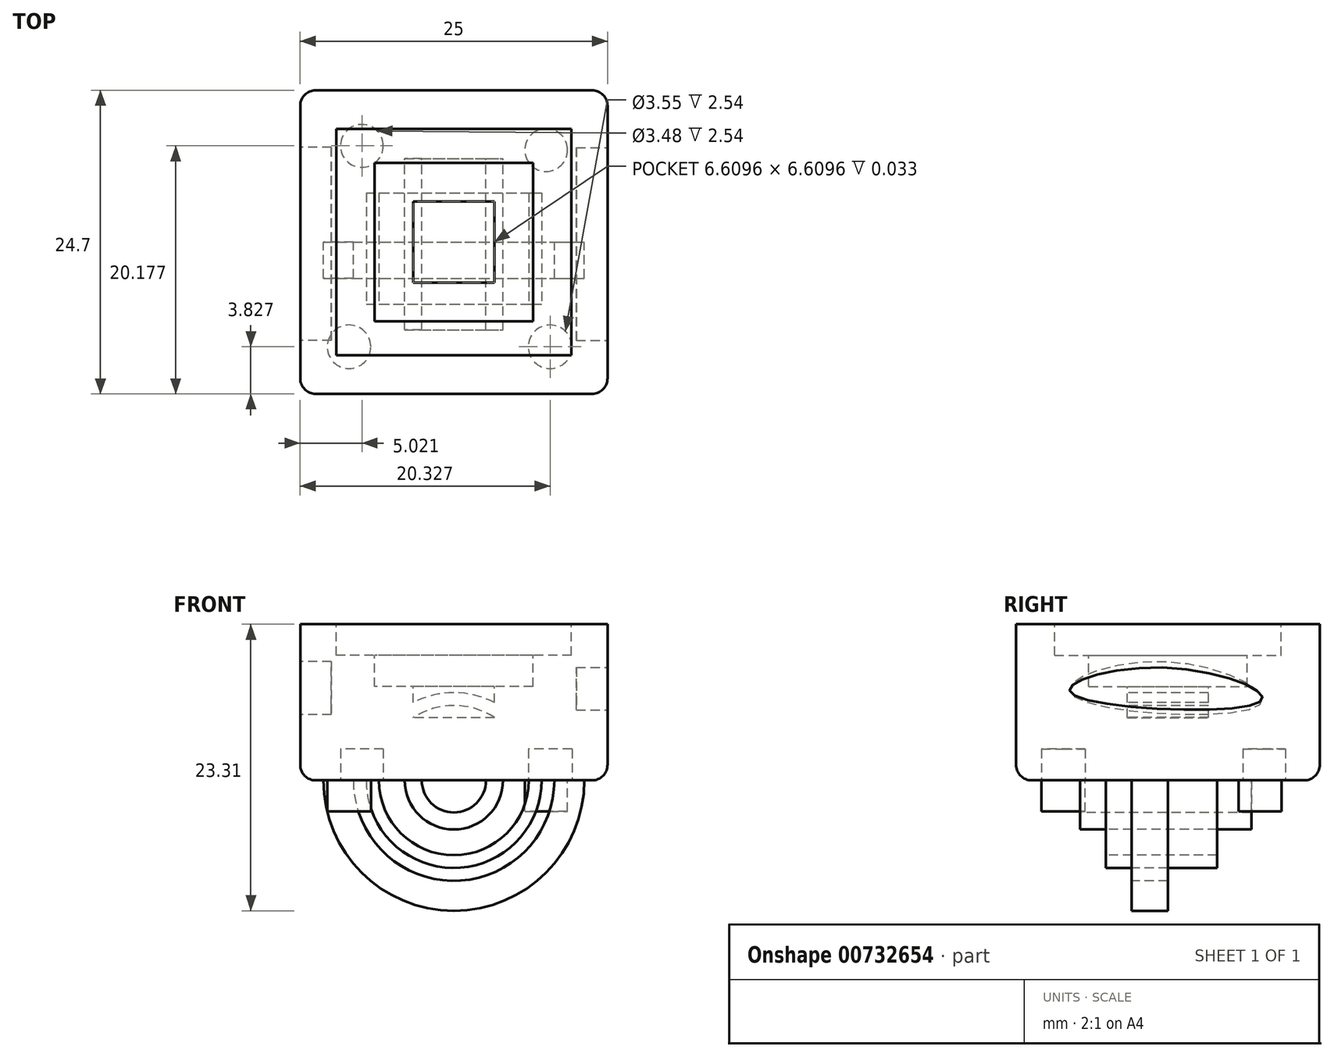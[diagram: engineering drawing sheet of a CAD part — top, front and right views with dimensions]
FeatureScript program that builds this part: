
annotation { "Feature Type Name" : "Feature", "Feature Type Description" : "" }
export const myFeature = defineFeature(function(context is Context, id is Id, definition is map)
    precondition{}
    {
        {
            var Q0;
            Q0=qCreatedBy(makeId("Top.planeOp"),FACE);
            var sketch = newSketch(context, id + "F0", { "sketchPlane" : qUnion([Q0])});
            skLineSegment(sketch, "E0.bottom", {"start": v(12.5, -12.35) * mm, "end": v(-12.5, -12.35) * mm});
            skLineSegment(sketch, "E0.top", {"start": v(12.5, 12.35) * mm, "end": v(-12.5, 12.35) * mm});
            skLineSegment(sketch, "E0.left", {"start": v(12.5, -12.35) * mm, "end": v(12.5, 12.35) * mm});
            skLineSegment(sketch, "E0.right", {"start": v(-12.5, -12.35) * mm, "end": v(-12.5, 12.35) * mm});
            skPoint(sketch, "E0.middle", {"position": v(0, 0) * mm});
            skSolve(sketch);
        }
        {
            var Q0;
            Q0=makeQuery(id+"F0.imprint","IMPRINT",FACE,{"disambiguationData":[TD([[makeQuery(id+"F0.imprint","IMPRINT",EDGE,{"derivedFrom":sQuery(id+"F0.wireOp",EDGE,"E0.bottom")}),-1.0]])]});
            extrude(context, id + "F1", {"entities" : qUnion([Q0]), "depth" : 12.7 * mm, "offsetDistance" : 25.4 * mm});
        }
        {
            var Q0;
            Q0=makeQuery(id+"F1.opExtrude","CAP_FACE",FACE,{"disambiguationData":[OSD([sQuery(id+"F0.wireOp",EDGE,"E0.bottom"),sQuery(id+"F0.wireOp",EDGE,"E0.top"),sQuery(id+"F0.wireOp",EDGE,"E0.left"),sQuery(id+"F0.wireOp",EDGE,"E0.right")])],"isStart":false});
            var sketch = newSketch(context, id + "F2", { "sketchPlane" : qUnion([Q0])});
            skLineSegment(sketch, "E1.bottom", {"start": v(9.57, -9.22) * mm, "end": v(-9.57, -9.22) * mm});
            skLineSegment(sketch, "E1.top", {"start": v(9.57, 9.22) * mm, "end": v(-9.57, 9.22) * mm});
            skLineSegment(sketch, "E1.left", {"start": v(9.57, -9.22) * mm, "end": v(9.57, 9.22) * mm});
            skLineSegment(sketch, "E1.right", {"start": v(-9.57, -9.22) * mm, "end": v(-9.57, 9.22) * mm});
            skPoint(sketch, "E1.middle", {"position": v(0, 0) * mm});
            skSolve(sketch);
        }
        {
            var Q0;
            Q0=makeQuery(id+"F2.imprint","IMPRINT",FACE,{"disambiguationData":[TD([[makeQuery(id+"F2.imprint","IMPRINT",EDGE,{"derivedFrom":sQuery(id+"F2.wireOp",EDGE,"E1.bottom")}),-1.0]])]});
            extrude(context, id + "F3", {"entities" : qUnion([Q0]), "operationType" : NewBodyOperationType.REMOVE, "oppositeDirection" : true, "depth" : 2.54 * mm, "offsetDistance" : 25.4 * mm});
        }
        {
            var Q0;
            Q0=makeQuery(id+"F3.boolean.opBoolean","COPY",FACE,{"derivedFrom":makeQuery(id+"F3.opExtrude","CAP_FACE",FACE,{"disambiguationData":[OSD([sQuery(id+"F2.wireOp",EDGE,"E1.bottom"),sQuery(id+"F2.wireOp",EDGE,"E1.top"),sQuery(id+"F2.wireOp",EDGE,"E1.left"),sQuery(id+"F2.wireOp",EDGE,"E1.right")])],"isStart":false})});
            var sketch = newSketch(context, id + "F4", { "sketchPlane" : qUnion([Q0])});
            skLineSegment(sketch, "E2.bottom", {"start": v(6.44, -6.44) * mm, "end": v(-6.44, -6.44) * mm});
            skLineSegment(sketch, "E2.top", {"start": v(6.44, 6.44) * mm, "end": v(-6.44, 6.44) * mm});
            skLineSegment(sketch, "E2.left", {"start": v(6.44, -6.44) * mm, "end": v(6.44, 6.44) * mm});
            skLineSegment(sketch, "E2.right", {"start": v(-6.44, -6.44) * mm, "end": v(-6.44, 6.44) * mm});
            skPoint(sketch, "E2.middle", {"position": v(0, 0) * mm});
            skSolve(sketch);
        }
        {
            var Q0;
            Q0=makeQuery(id+"F4.imprint","IMPRINT",FACE,{"disambiguationData":[TD([[makeQuery(id+"F4.imprint","IMPRINT",EDGE,{"derivedFrom":sQuery(id+"F4.wireOp",EDGE,"E2.bottom")}),-1.0]])]});
            extrude(context, id + "F5", {"entities" : qUnion([Q0]), "operationType" : NewBodyOperationType.REMOVE, "oppositeDirection" : true, "depth" : 2.54 * mm, "offsetDistance" : 25.4 * mm});
        }
        {
            var Q0;
            Q0=makeQuery(id+"F5.boolean.opBoolean","COPY",FACE,{"derivedFrom":makeQuery(id+"F5.opExtrude","CAP_FACE",FACE,{"disambiguationData":[OSD([sQuery(id+"F4.wireOp",EDGE,"E2.bottom"),sQuery(id+"F4.wireOp",EDGE,"E2.top"),sQuery(id+"F4.wireOp",EDGE,"E2.left"),sQuery(id+"F4.wireOp",EDGE,"E2.right")])],"isStart":false})});
            var sketch = newSketch(context, id + "F6", { "sketchPlane" : qUnion([Q0])});
            skLineSegment(sketch, "E3.bottom", {"start": v(3.3, -3.3) * mm, "end": v(-3.3, -3.3) * mm});
            skLineSegment(sketch, "E3.top", {"start": v(3.3, 3.3) * mm, "end": v(-3.3, 3.3) * mm});
            skLineSegment(sketch, "E3.left", {"start": v(3.3, -3.3) * mm, "end": v(3.3, 3.3) * mm});
            skLineSegment(sketch, "E3.right", {"start": v(-3.3, -3.3) * mm, "end": v(-3.3, 3.3) * mm});
            skPoint(sketch, "E3.middle", {"position": v(0, 0) * mm});
            skSolve(sketch);
        }
        {
            var Q0;
            Q0=makeQuery(id+"F6.imprint","IMPRINT",FACE,{"disambiguationData":[TD([[makeQuery(id+"F6.imprint","IMPRINT",EDGE,{"derivedFrom":sQuery(id+"F6.wireOp",EDGE,"E3.bottom")}),-1.0]])]});
            extrude(context, id + "F7", {"entities" : qUnion([Q0]), "operationType" : NewBodyOperationType.REMOVE, "oppositeDirection" : true, "depth" : 2.54 * mm, "offsetDistance" : 25.4 * mm});
        }
        {
            var Q0;
            Q0=qCreatedBy(makeId("Top.planeOp"),FACE);
            var sketch = newSketch(context, id + "F8", { "sketchPlane" : qUnion([Q0])});
            skLineSegment(sketch, "E4", {"start": v(0, -12) * mm, "end": v(0, 11.65) * mm});
            skLineSegment(sketch, "E5.bottom", {"start": v(2.6, -7.13) * mm, "end": v(4, -7.13) * mm});
            skLineSegment(sketch, "E5.top", {"start": v(2.6, 6.78) * mm, "end": v(4, 6.78) * mm});
            skLineSegment(sketch, "E5.left", {"start": v(2.6, -7.13) * mm, "end": v(2.6, 6.78) * mm});
            skLineSegment(sketch, "E5.right", {"start": v(4, -7.13) * mm, "end": v(4, 6.78) * mm});
            skSolve(sketch);
        }
        {
            var Q0;
            Q0=makeQuery(id+"F8.imprint","IMPRINT",FACE,{"disambiguationData":[TD([[makeQuery(id+"F8.imprint","IMPRINT",EDGE,{"derivedFrom":sQuery(id+"F8.wireOp",EDGE,"E5.bottom")}),1.0]])]});
            var Q1;
            Q1=sQuery(id+"F8.wireOp",EDGE,"E4");
            revolve(context, id + "F9", {"operationType" : NewBodyOperationType.ADD, "surfaceOperationType" : NewSurfaceOperationType.NEW, "entities" : qUnion([Q0]), "axis" : qUnion([Q1]), "revolveType" : RevolveType.ONE_DIRECTION, "angle" : 180 * degree});
        }
        {
            var Q0;
            Q0=qCreatedBy(makeId("Top.planeOp"),FACE);
            var sketch = newSketch(context, id + "F10", { "sketchPlane" : qUnion([Q0])});
            skLineSegment(sketch, "E6", {"start": v(0, -13.4) * mm, "end": v(0, 11.65) * mm});
            skLineSegment(sketch, "E7.bottom", {"start": v(6.09, -5.04) * mm, "end": v(7.13, -5.04) * mm});
            skLineSegment(sketch, "E7.top", {"start": v(6.09, 4) * mm, "end": v(7.13, 4) * mm});
            skLineSegment(sketch, "E7.left", {"start": v(6.09, -5.04) * mm, "end": v(6.09, 4) * mm});
            skLineSegment(sketch, "E7.right", {"start": v(7.13, -5.04) * mm, "end": v(7.13, 4) * mm});
            skSolve(sketch);
        }
        {
            var Q0;
            Q0=makeQuery(id+"F10.imprint","IMPRINT",FACE,{"disambiguationData":[TD([[makeQuery(id+"F10.imprint","IMPRINT",EDGE,{"derivedFrom":sQuery(id+"F10.wireOp",EDGE,"E7.bottom")}),1.0]])]});
            var Q1;
            Q1=sQuery(id+"F10.wireOp",EDGE,"E6");
            revolve(context, id + "F11", {"operationType" : NewBodyOperationType.ADD, "surfaceOperationType" : NewSurfaceOperationType.NEW, "entities" : qUnion([Q0]), "axis" : qUnion([Q1]), "revolveType" : RevolveType.FULL});
        }
        {
            var Q0;
            Q0=qCreatedBy(makeId("Top.planeOp"),FACE);
            var sketch = newSketch(context, id + "F12", { "sketchPlane" : qUnion([Q0])});
            skLineSegment(sketch, "E8.bottom", {"start": v(8.17, -2.96) * mm, "end": v(10.61, -2.96) * mm});
            skLineSegment(sketch, "E8.top", {"start": v(8.17, 0) * mm, "end": v(10.61, 0) * mm});
            skLineSegment(sketch, "E8.left", {"start": v(8.17, -2.96) * mm, "end": v(8.17, 0) * mm});
            skLineSegment(sketch, "E8.right", {"start": v(10.61, -2.96) * mm, "end": v(10.61, 0) * mm});
            skLineSegment(sketch, "E9", {"start": v(0, -13.4) * mm, "end": v(0, 12.35) * mm});
            skSolve(sketch);
        }
        {
            var Q0;
            Q0=makeQuery(id+"F12.imprint","IMPRINT",FACE,{"disambiguationData":[TD([[makeQuery(id+"F12.imprint","IMPRINT",EDGE,{"derivedFrom":sQuery(id+"F12.wireOp",EDGE,"E8.bottom")}),1.0]])]});
            var Q1;
            Q1=sQuery(id+"F12.wireOp",EDGE,"E9");
            revolve(context, id + "F13", {"operationType" : NewBodyOperationType.ADD, "surfaceOperationType" : NewSurfaceOperationType.NEW, "entities" : qUnion([Q0]), "axis" : qUnion([Q1]), "revolveType" : RevolveType.ONE_DIRECTION, "angle" : 180 * degree});
        }
        {
            var Q0;
            Q0=makeQuery(id+"F1.opExtrude","CAP_EDGE",EDGE,{"disambiguationData":[OSD([sQuery(id+"F0.wireOp",EDGE,"E0.bottom")])],"isStart":true});
            fillet(context, id + "F14", {"entities" : qUnion([Q0]), "radius" : 1.27 * mm, "tangentPropagation" : true, "allowEdgeOverflow" : false});
        }
        {
            var Q0;
            Q0=makeQuery(id+"F1.opExtrude","CAP_EDGE",EDGE,{"disambiguationData":[OSD([sQuery(id+"F0.wireOp",EDGE,"E0.right")])],"isStart":true});
            fillet(context, id + "F15", {"entities" : qUnion([Q0]), "radius" : 1.27 * mm, "tangentPropagation" : true, "allowEdgeOverflow" : false});
        }
        {
            var Q0;
            Q0=makeQuery(id+"F1.opExtrude","CAP_EDGE",EDGE,{"disambiguationData":[OSD([sQuery(id+"F0.wireOp",EDGE,"E0.top")])],"isStart":true});
            fillet(context, id + "F16", {"entities" : qUnion([Q0]), "radius" : 1.27 * mm, "tangentPropagation" : true, "allowEdgeOverflow" : false});
        }
        {
            var Q0;
            Q0=makeQuery(id+"F1.opExtrude","CAP_EDGE",EDGE,{"disambiguationData":[OSD([sQuery(id+"F0.wireOp",EDGE,"E0.left")])],"isStart":true});
            fillet(context, id + "F17", {"entities" : qUnion([Q0]), "radius" : 1.27 * mm, "tangentPropagation" : true, "allowEdgeOverflow" : false});
        }
        {
            var Q0;
            Q0=qCreatedBy(makeId("Top.planeOp"),FACE);
            var sketch = newSketch(context, id + "F18", { "sketchPlane" : qUnion([Q0])});
            skCircle(sketch, "E10", {"center": v(-8.52, -8.52) * mm, "radius": 1.77 * mm});
            skCircle(sketch, "E11", {"center": v(7.83, -8.52) * mm, "radius": 1.77 * mm});
            skCircle(sketch, "E12", {"center": v(-7.48, 7.83) * mm, "radius": 1.74 * mm});
            skCircle(sketch, "E13", {"center": v(7.5, 7.49) * mm, "radius": 1.74 * mm});
            skSolve(sketch);
        }
        {
            var Q0;
            Q0=makeQuery(id+"F18.imprint","IMPRINT",FACE,{"disambiguationData":[TD([[makeQuery(id+"F18.imprint","IMPRINT",EDGE,{"derivedFrom":sQuery(id+"F18.wireOp",EDGE,"E10")}),1.0]])]});
            var Q1;
            Q1=makeQuery(id+"F18.imprint","IMPRINT",FACE,{"disambiguationData":[TD([[makeQuery(id+"F18.imprint","IMPRINT",EDGE,{"derivedFrom":sQuery(id+"F18.wireOp",EDGE,"E13")}),1.0]])]});
            extrude(context, id + "F19", {"entities" : qUnion([Q0, Q1]), "operationType" : NewBodyOperationType.ADD, "oppositeDirection" : true, "depth" : 2.54 * mm, "offsetDistance" : 25.4 * mm});
        }
        {
            var Q0;
            Q0=makeQuery(id+"F18.imprint","IMPRINT",FACE,{"disambiguationData":[TD([[makeQuery(id+"F18.imprint","IMPRINT",EDGE,{"derivedFrom":sQuery(id+"F18.wireOp",EDGE,"E12")}),1.0]])]});
            var Q1;
            Q1=makeQuery(id+"F18.imprint","IMPRINT",FACE,{"disambiguationData":[TD([[makeQuery(id+"F18.imprint","IMPRINT",EDGE,{"derivedFrom":sQuery(id+"F18.wireOp",EDGE,"E11")}),1.0]])]});
            extrude(context, id + "F20", {"entities" : qUnion([Q0, Q1]), "operationType" : NewBodyOperationType.REMOVE, "depth" : 2.54 * mm, "offsetDistance" : 25.4 * mm});
        }
        {
            var Q0;
            Q0=makeQuery(id+"F1.opExtrude","SWEPT_FACE",FACE,{"disambiguationData":[OSD([sQuery(id+"F0.wireOp",EDGE,"E0.left")])]});
            var sketch = newSketch(context, id + "F21", { "sketchPlane" : qUnion([Q0])});
            skFitSpline(sketch, "E14", {"points": [v(7.48, 6.38) * mm, v(0, 9.16) * mm, v(-7.83, 7.06) * mm, v(7.48, 6.38) * mm]});
            skSolve(sketch);
        }
        {
            var Q0;
            Q0=makeQuery(id+"F21.imprint","IMPRINT",FACE,{"disambiguationData":[TD([[makeQuery(id+"F21.imprint","IMPRINT",EDGE,{"derivedFrom":sQuery(id+"F21.wireOp",EDGE,"E14")}),1.0]])]});
            extrude(context, id + "F22", {"entities" : qUnion([Q0]), "operationType" : NewBodyOperationType.REMOVE, "oppositeDirection" : true, "depth" : 2.54 * mm, "offsetDistance" : 25.4 * mm});
        }
        {
            var Q0;
            Q0=makeQuery(id+"F1.opExtrude","SWEPT_FACE",FACE,{"disambiguationData":[OSD([sQuery(id+"F0.wireOp",EDGE,"E0.right")])]});
            var sketch = newSketch(context, id + "F23", { "sketchPlane" : qUnion([Q0])});
            skPoint(sketch, "E15.1.internal.snap0", {"position": v(0, 12.7) * mm});
            skPoint(sketch, "E15.2.internal.snap0", {"position": v(11.08, 6.99) * mm});
            skFitSpline(sketch, "E15", {"points": [v(-7.48, 6.16) * mm, v(0, 9.63) * mm, v(7.83, 6.99) * mm, v(-7.48, 6.16) * mm]});
            skSolve(sketch);
        }
        {
            var Q0;
            Q0=makeQuery(id+"F23.imprint","IMPRINT",FACE,{"disambiguationData":[TD([[makeQuery(id+"F23.imprint","IMPRINT",EDGE,{"derivedFrom":sQuery(id+"F23.wireOp",EDGE,"E15")}),-1.0]])]});
            extrude(context, id + "F24", {"entities" : qUnion([Q0]), "operationType" : NewBodyOperationType.REMOVE, "oppositeDirection" : true, "depth" : 2.54 * mm, "offsetDistance" : 25.4 * mm});
        }
    });
